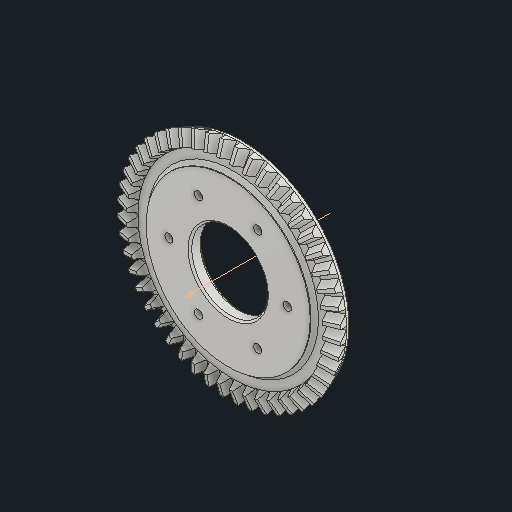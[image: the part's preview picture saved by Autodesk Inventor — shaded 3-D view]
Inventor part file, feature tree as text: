
AUTODESK INVENTOR PART (.ipt)
format: ipt  version: 2022 (Build 260153000, 153)  size: 861,184 bytes
history: native  units: mm
features: other x26, sketch x5, chamfer x4, extrude x3, reference x3, loft x2, pattern_circular x2, plane x2, hole x1, projected_geometry x1
ambient origin geometry x6: Origin, XZ Plane, X Axis, Y Axis, Z Axis, Center Point
bodies: Solid1 (feature_tree)
feature tree (49):
  other  "Top Point"
  other  "Mesh Plane2"
  other  "Teeth Body"
  other  "Start Point"
  other  "Tooth Plane"
  other  "Start Sketch"
  other  "End Point"
  other  "3D Sketch Right"
  other  "End Plane Right"
  loft  "Loft Right"
  pattern_circular  "Circular Pattern Right"  [2 undecoded]
  other  "3D Sketch Left"
  other  "End Plane Left"
  loft  "Loft Left"
  pattern_circular  "Circular Pattern Left"  [2 undecoded]
  other  "Fix Body"
  plane  "Work Plane6"
  extrude  "Extrusion4"  Depth=4.6mm
  sketch  "Sketch17"  dims[d3=8.0mm]
  plane  "Work Plane9"
  extrude  "Extrusion9"  Depth=4.6mm
  chamfer  "Chamfer6"  Distance=50.049398mm
  chamfer  "Chamfer7"  Distance=124.522644mm
  extrude  "Extrusion10"  TaperAngle=0.0deg  [1 undecoded]
  chamfer  "Chamfer8"  Distance=480.0mm Angle=90.0deg
  hole  "Hole2"  [1 undecoded]
  chamfer  "Chamfer9"  Distance=357.584802mm
  other  "Mesh Plane"
  other  "Top Plane"
  other  "Teeth Body Sketch"
  other  "End Plane"
  other  "End Sketch"
  other  "Helical Curve Left"
  other  "End Sketch Left"
  other  "Body Sketch"
  sketch  "Sketch6"  dims[d0=120.0mm d1=118.488225mm]
  other  "Srf1"
  other  "Helical Curve Right"
  other  "End Sketch Right"
  sketch  "Sketch11"  dims[d2=122.536758mm]
  reference  "Reference9"
  reference  "Reference11"
  sketch  "Sketch19"  dims[d4=20.545674mm]
  projected_geometry  "Projected Loop5"
  sketch  "Sketch20"  dims[d5=90.0deg d7=59.301777mm d8=57.411626mm d9=142.839828mm d11=8.275mm d12=51.697165mm d15=50.049398mm d16=124.522644mm d17=0.0mm d18=90.0deg d19=0.0mm d20=90.0deg d21=480.0mm d22=360.0deg d26=357.584802mm d27=3.045601mm d28=120.0mm d29=-11.938871mm d30=51.697165mm d31=50.049398mm d32=124.522644mm d35=0.0mm d37=0.0mm d39=0.0mm d40=90.0deg d41=480.0mm d42=360.0deg d46=90.0deg d47=90.0deg d48=0.0mm d49=0.0mm d50=90.0deg d51=0.654498mm d52=0.0mm d53=0.0mm d54=0.0mm d56=19.770163mm d57=168.118244mm d58=160.308244mm d59=146.559461mm d60=139.750983mm d61=146.559461mm d62=139.750983mm d65=357.584802mm d66=31.5mm d67=120.0mm d68=-11.938871mm d69=3.045601mm d70=50.049398mm d71=124.522644mm d72=51.697165mm d73=139.750983mm d74=146.559461mm d75=0.0mm d77=0.0mm d79=0.0mm d80=90.0deg d81=480.0mm d82=360.0deg d84=10.0mm d85=20.0mm d86=20.0mm d87=10.0mm d88=0.0mm d89=0.0mm d90=90.0deg d91=90.0deg d92=90.0deg d93=90.0deg d103=0.0mm d104=0.0mm d138=42.0mm d139=5.0mm d140=10.0mm d141=0.0mm d142=2.0mm d143=2.0mm d144=45.0deg d145=1.0mm d146=2.0mm d147=45.0deg d148=2.0mm d149=0.0mm d150=2.0mm d151=2.0mm d152=3.490659mm d153=4.5mm d154=5.0mm d155=8.0mm d156=4.6mm d157=90.0deg d158=5.8mm d159=20.594885mm d160=2.0mm d161=2.0mm d162=3.490659mm d106=0.5mm d107=0.872665mm d108=0.5mm d109=0.872665mm d128=1.0mm d129=1.0mm d130=8.8mm d131=0.15mm d132=0.25mm d133=0.375mm d134=14.3117mm d135=6.0mm d136=20.594885mm d137=0.0625mm]
  reference  "Reference13"
  other  "Pitch Diameter"
  other  "SistemaElevacionV2.iam"
  other  "Tuerca3:1"
note: 6 required parameter values undecoded (feature->parameter linkage not recoverable at this tier; creation-order binding heuristic only, values carry confidence <= 0.55)
